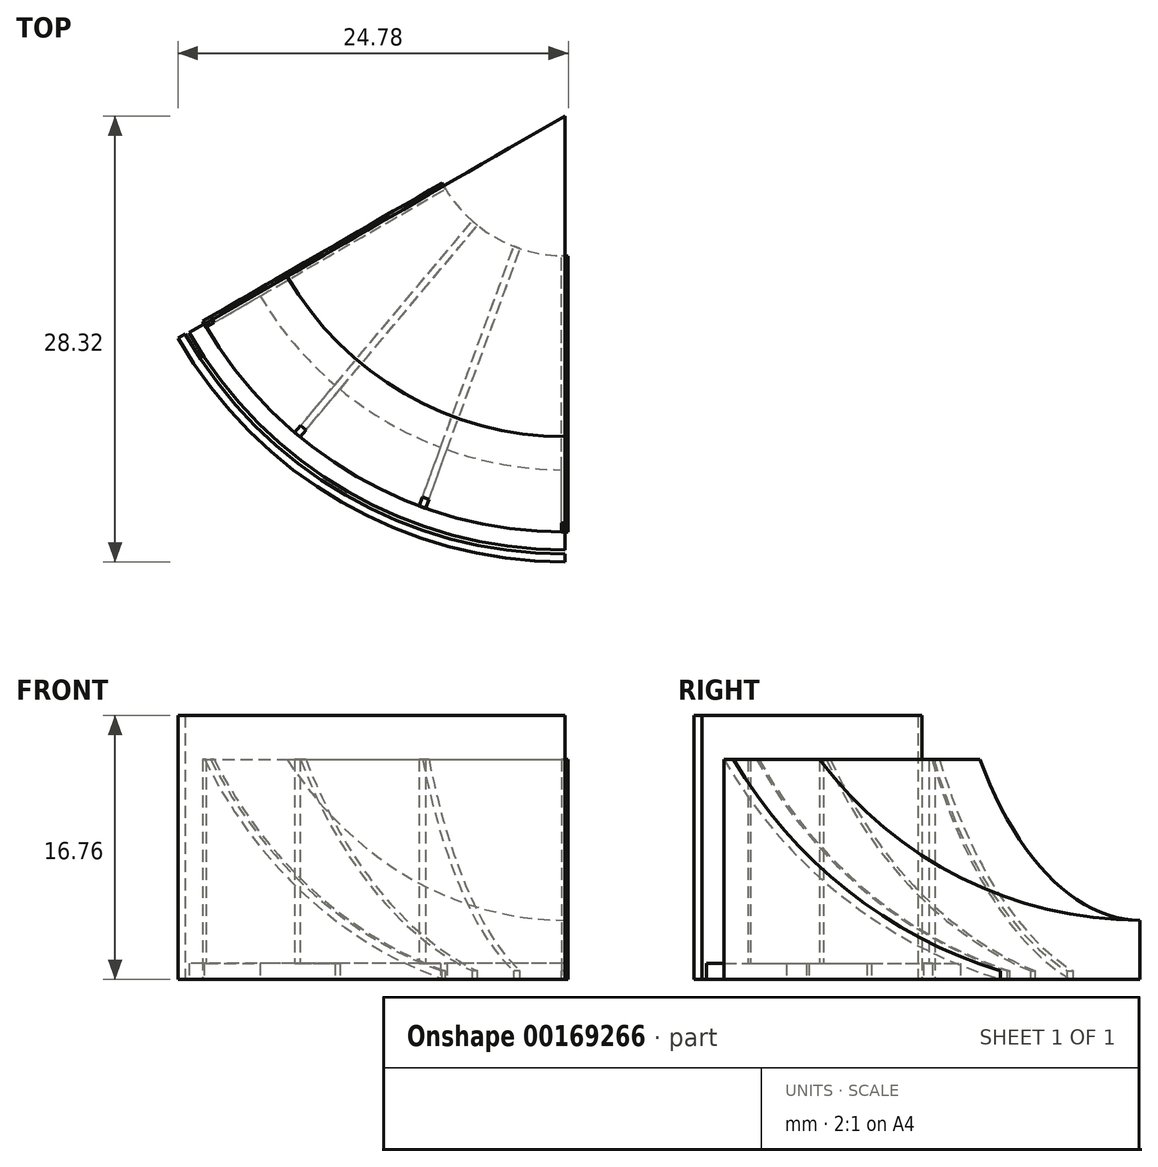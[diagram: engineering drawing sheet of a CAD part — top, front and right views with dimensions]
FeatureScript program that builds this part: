
annotation { "Feature Type Name" : "Feature", "Feature Type Description" : "" }
export const myFeature = defineFeature(function(context is Context, id is Id, definition is map)
    precondition{}
    {
        {
            var Q0;
            Q0=qCreatedBy(makeId("Right.planeOp"),FACE);
            var sketch = newSketch(context, id + "F0", { "sketchPlane" : qUnion([Q0])});
            skArc(sketch, "E0", {"start": v(-20.36, -15.19) * mm, "mid": v(-11.39, -22.7) * mm, "end": v(0, -25.4) * mm});
            skArc(sketch, "E1", {"start": v(-26.43, -15.19) * mm, "mid": v(-18.98, -23.85) * mm, "end": v(-8.88, -29.16) * mm});
            skLineSegment(sketch, "E2", {"start": v(-8.88, -29.16) * mm, "end": v(0, -29.16) * mm});
            skLineSegment(sketch, "E3.0", {"start": v(-26.43, -15.19) * mm, "end": v(-20.36, -15.19) * mm});
            skLineSegment(sketch, "E4", {"start": v(0, 0) * mm, "end": v(0, -29.16) * mm, "construction": true});
            skLineSegment(sketch, "E5", {"start": v(0, -25.4) * mm, "end": v(0, -29.16) * mm});
            skLineSegment(sketch, "E6", {"start": v(-26.43, -15.19) * mm, "end": v(-11.97, -40.33) * mm, "construction": true});
            skSolve(sketch);
        }
        {
            var Q0;
            Q0 = qSketchRegion(id + "F0", true);
            var Q1;
            Q1=sQuery(id+"F0.wireOp",EDGE,"E4");
            revolve(context, id + "F1", {"entities" : qUnion([Q0]), "axis" : qUnion([Q1]), "revolveType" : RevolveType.ONE_DIRECTION, "angle" : 60 * degree});
        }
        {
            var Q0;
            Q0=makeQuery(id+"F1.opRevolve","CAP_FACE",FACE,{"disambiguationData":[OSD([sQuery(id+"F0.wireOp",EDGE,"E0"),sQuery(id+"F0.wireOp",EDGE,"E1"),sQuery(id+"F0.wireOp",EDGE,"E2"),sQuery(id+"F0.wireOp",EDGE,"E3.0"),sQuery(id+"F0.wireOp",EDGE,"E5")])],"isStart":true});
            var sketch = newSketch(context, id + "F2", { "sketchPlane" : qUnion([Q0])});
            skArc(sketch, "E7.0", {"start": v(-26.43, -15.19) * mm, "mid": v(-18.98, -23.85) * mm, "end": v(-8.88, -29.16) * mm});
            skLineSegment(sketch, "E8", {"start": v(-26.43, -15.19) * mm, "end": v(-26.43, -29.16) * mm});
            skLineSegment(sketch, "E9", {"start": v(-26.43, -29.16) * mm, "end": v(-8.88, -29.16) * mm});
            skLineSegment(sketch, "E10.0", {"start": v(0, 0) * mm, "end": v(0, -25.4) * mm, "construction": true});
            skLineSegment(sketch, "E11.0.1", {"start": v(-25.84, -15.19) * mm, "end": v(-26.43, -15.19) * mm});
            skArc(sketch, "E11.0.2", {"start": v(-26.43, -15.19) * mm, "mid": v(-18.98, -23.85) * mm, "end": v(-8.88, -29.16) * mm, "construction": true});
            skLineSegment(sketch, "E11.0.4", {"start": v(0, -29.16) * mm, "end": v(0, -25.4) * mm});
            skArc(sketch, "E12.0", {"start": v(-25.84, -15.19) * mm, "mid": v(-18.61, -23.5) * mm, "end": v(-8.88, -28.63) * mm});
            skLineSegment(sketch, "E13", {"start": v(-8.88, -29.16) * mm, "end": v(-8.88, -28.63) * mm});
            skPoint(sketch, "E11.0.0.end.orphan", {"position": v(-20.36, -15.19) * mm});
            skPoint(sketch, "E14.orphan", {"position": v(0, -29.16) * mm});
            skSolve(sketch);
        }
        {
            var Q0;
            Q0 = qSketchRegion(id + "F2", true);
            extrude(context, id + "F3", {"entities" : qUnion([Q0]), "depth" : 0.43 * mm, "symmetric" : true});
        }
        {
            var Q0;
            Q0=makeQuery(id+"F3.opExtrude","SWEPT_BODY",BODY,{"disambiguationData":[OSD([sQuery(id+"F2.wireOp",EDGE,"E8"),sQuery(id+"F2.wireOp",EDGE,"E9"),sQuery(id+"F2.wireOp",EDGE,"E11.0.1"),sQuery(id+"F2.wireOp",EDGE,"E12.0"),sQuery(id+"F2.wireOp",EDGE,"E13")])]});
            var Q1;
            Q1=sQuery(id+"F0.wireOp",EDGE,"E4");
            circularPattern(context, id + "F4", {"entities" : qUnion([Q0]), "axis" : qUnion([Q1]), "angle" : 60 * degree, "instanceCount" : 4, "equalSpace" : true});
        }
        {
            var Q0;
            Q0=makeQuery(id+"F1.opRevolve","SWEPT_FACE",FACE,{"disambiguationData":[OSD([sQuery(id+"F0.wireOp",EDGE,"E2")])]});
            var sketch = newSketch(context, id + "F5", { "sketchPlane" : qUnion([Q0])});
            skArc(sketch, "E15", {"start": v(0, 27.55) * mm, "mid": v(-13.78, 23.85) * mm, "end": v(-23.87, 13.76) * mm});
            skArc(sketch, "E16.0", {"start": v(0, 22.47) * mm, "mid": v(-11.24, 19.45) * mm, "end": v(-19.46, 11.22) * mm});
            skLineSegment(sketch, "E17", {"start": v(0, 22.47) * mm, "end": v(0, 27.55) * mm});
            skLineSegment(sketch, "E18", {"start": v(-19.46, 11.22) * mm, "end": v(-23.87, 13.76) * mm});
            skSolve(sketch);
        }
        {
            var Q0;
            Q0 = qSketchRegion(id + "F5", true);
            extrude(context, id + "F6", {"entities" : qUnion([Q0]), "operationType" : NewBodyOperationType.ADD, "oppositeDirection" : true, "depth" : 1.02 * mm});
        }
        {
            var Q0;
            {var subQ0=makeQuery(id+"F3.opExtrude","SWEPT_FACE",FACE,{"disambiguationData":[OSD([sQuery(id+"F2.wireOp",EDGE,"E9")])]});Q0=makeQuery(id+"F6.boolean.opBoolean","MERGE",FACE,{"derivedFrom":[subQ0,makeQuery(id+"F4.opPattern","COPY",FACE,{"derivedFrom":subQ0,"instanceName":"1"}),makeQuery(id+"F4.opPattern","COPY",FACE,{"derivedFrom":subQ0,"instanceName":"2"}),makeQuery(id+"F4.opPattern","COPY",FACE,{"derivedFrom":subQ0,"instanceName":"3"}),makeQuery(id+"F4.opPattern","COPY",FACE,{"derivedFrom":subQ0,"instanceName":"4"}),makeQuery(id+"F4.opPattern","COPY",FACE,{"derivedFrom":subQ0,"instanceName":"5"}),makeQuery(id+"F4.opPattern","COPY",FACE,{"derivedFrom":subQ0,"instanceName":"6"}),makeQuery(id+"F6.opExtrude","CAP_FACE",FACE,{"disambiguationData":[OSD([sQuery(id+"F5.wireOp",EDGE,"E15"),sQuery(id+"F5.wireOp",EDGE,"E16.0"),sQuery(id+"F5.wireOp",EDGE,"E17"),sQuery(id+"F5.wireOp",EDGE,"E18")])],"isStart":true})]});}
            var sketch = newSketch(context, id + "F7", { "sketchPlane" : qUnion([Q0])});
            skLineSegment(sketch, "E19", {"start": v(0, 0) * mm, "end": v(0, 30.89) * mm});
            skArc(sketch, "E20", {"start": v(0, 28.32) * mm, "mid": v(-14.19, 24.5) * mm, "end": v(-24.56, 14.1) * mm});
            skArc(sketch, "E21.0", {"start": v(0, 27.81) * mm, "mid": v(-13.93, 24.07) * mm, "end": v(-24.12, 13.85) * mm});
            skLineSegment(sketch, "E22", {"start": v(-24.12, 13.85) * mm, "end": v(-24.56, 14.1) * mm});
            skLineSegment(sketch, "E23", {"start": v(0, 27.81) * mm, "end": v(0, 28.32) * mm});
            skSolve(sketch);
        }
        {
            var Q0;
            Q0 = qSketchRegion(id + "F7", true);
            extrude(context, id + "F8", {"entities" : qUnion([Q0]), "operationType" : NewBodyOperationType.ADD, "oppositeDirection" : true, "depth" : 16.76 * mm});
        }
    });
